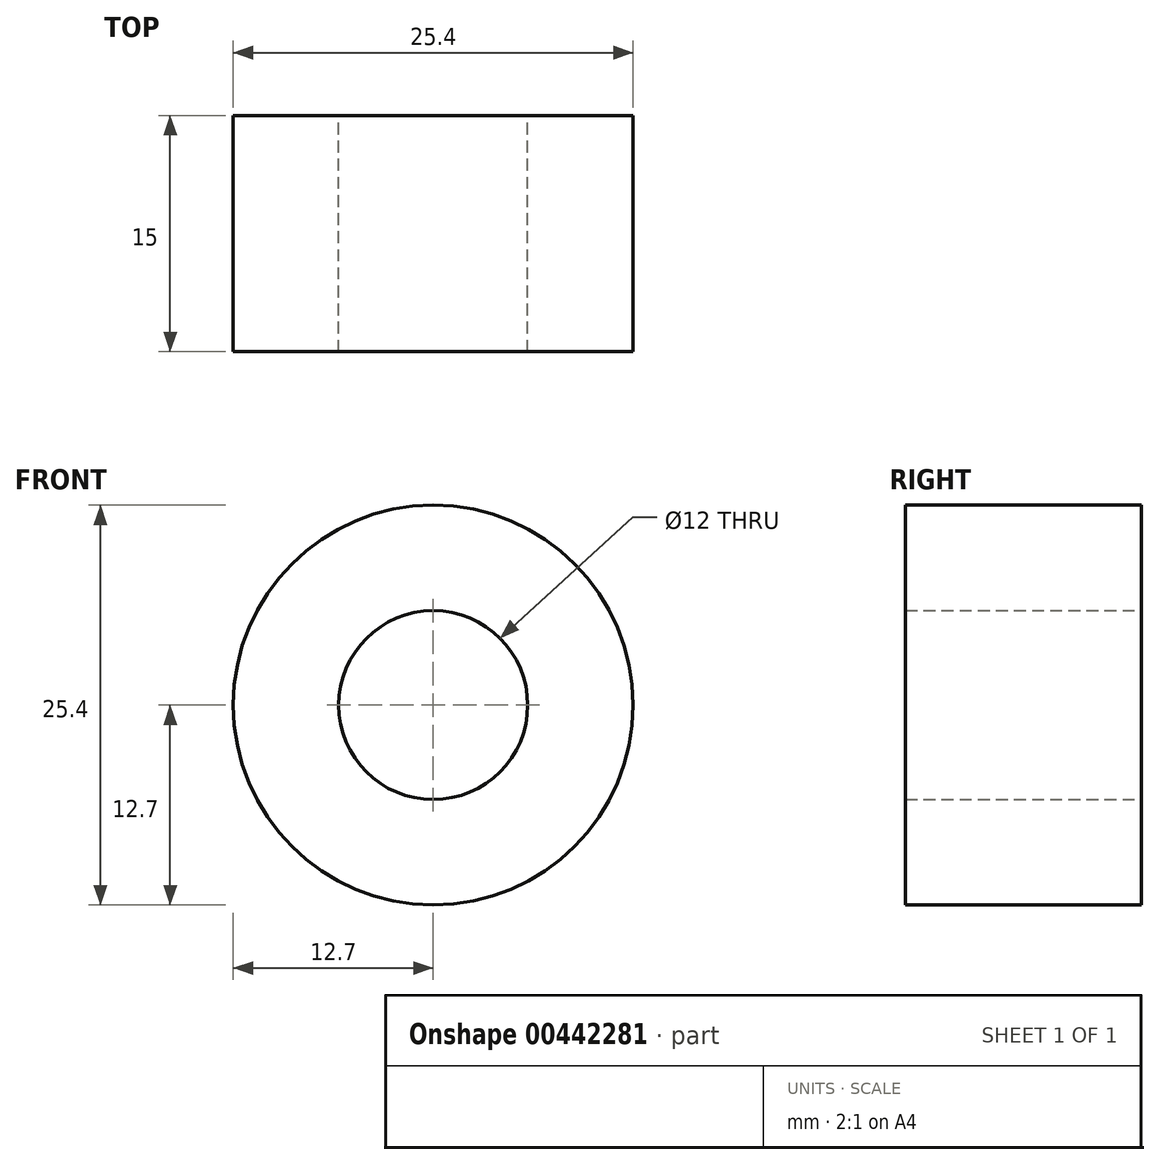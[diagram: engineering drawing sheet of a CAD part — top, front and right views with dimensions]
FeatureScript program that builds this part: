
annotation { "Feature Type Name" : "Feature", "Feature Type Description" : "" }
export const myFeature = defineFeature(function(context is Context, id is Id, definition is map)
    precondition{}
    {
        {
            var Q0;
            Q0=qCreatedBy(makeId("Front.planeOp"),FACE);
            var sketch = newSketch(context, id + "F0", { "sketchPlane" : qUnion([Q0])});
            skCircle(sketch, "E0", {"center": v(0, 0) * mm, "radius": 6 * mm});
            skCircle(sketch, "E1", {"center": v(0, 0) * mm, "radius": 12.7 * mm});
            skSolve(sketch);
        }
        {
            var Q0;
            Q0 = qSketchRegion(id + "F0", true);
            var Q1;
            Q1 = qConstructionFilter(qBodyType(qCreatedBy(id + "F0" ,EDGE), BodyType.WIRE), ConstructionObject.NO);
            extrude(context, id + "F1", {"entities" : qUnion([Q0]), "flatOperationType" : FlatOperationType.REMOVE, "surfaceEntities" : qUnion([Q1]), "endBound" : BoundingType.SYMMETRIC, "offsetDistance" : 25 * mm, "depth" : 15 * mm, "domain" : OperationDomain.MODEL});
        }
    });
